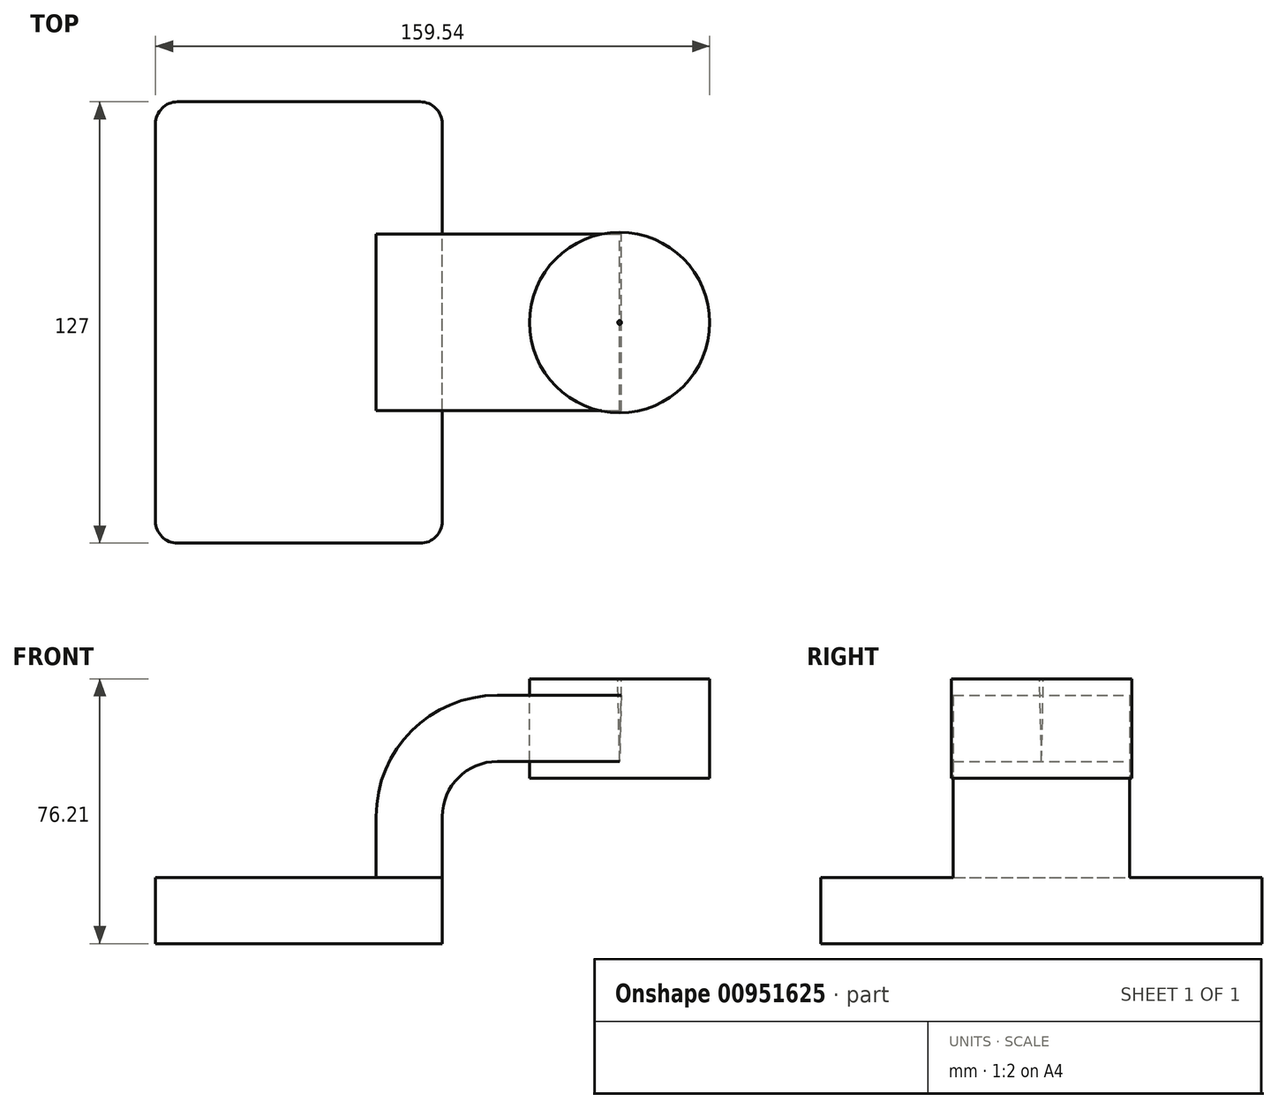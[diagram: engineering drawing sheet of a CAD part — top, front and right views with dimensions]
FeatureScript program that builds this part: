
annotation { "Feature Type Name" : "Feature", "Feature Type Description" : "" }
export const myFeature = defineFeature(function(context is Context, id is Id, definition is map)
    precondition{}
    {
        {
            var Q0;
            Q0=qCreatedBy(makeId("Front.planeOp"),FACE);
            var sketch = newSketch(context, id + "F0", { "sketchPlane" : qUnion([Q0])});
            skLineSegment(sketch, "E0.bottom", {"start": v(41.27, 9.53) * mm, "end": v(-41.28, 9.53) * mm});
            skLineSegment(sketch, "E0.top", {"start": v(41.28, -9.52) * mm, "end": v(-41.27, -9.52) * mm});
            skLineSegment(sketch, "E0.left", {"start": v(41.28, 9.53) * mm, "end": v(41.28, -9.52) * mm});
            skLineSegment(sketch, "E0.right", {"start": v(-41.28, 9.53) * mm, "end": v(-41.27, -9.52) * mm});
            skPoint(sketch, "E0.middle", {"position": v(0, 0) * mm});
            skLineSegment(sketch, "E1.bottom", {"start": v(118.27, 66.68) * mm, "end": v(67.47, 66.68) * mm});
            skLineSegment(sketch, "E1.top", {"start": v(118.27, 38.1) * mm, "end": v(67.47, 38.1) * mm});
            skLineSegment(sketch, "E1.left", {"start": v(118.27, 66.68) * mm, "end": v(118.27, 38.1) * mm});
            skLineSegment(sketch, "E1.right", {"start": v(67.47, 66.68) * mm, "end": v(67.47, 38.1) * mm});
            skPoint(sketch, "E1.middle", {"position": v(92.87, 52.39) * mm});
            skLineSegment(sketch, "E2", {"start": v(41.27, 9.53) * mm, "end": v(41.27, 27) * mm});
            skArc(sketch, "E3", {"start": v(41.27, 27) * mm, "mid": v(45.92, 38.23) * mm, "end": v(57.15, 42.88) * mm});
            skLineSegment(sketch, "E4", {"start": v(57.15, 42.88) * mm, "end": v(92.33, 42.88) * mm});
            skLineSegment(sketch, "E5.0", {"start": v(57.15, 61.93) * mm, "end": v(92.87, 61.93) * mm});
            skArc(sketch, "E5.1", {"start": v(22.23, 27) * mm, "mid": v(32.45, 51.7) * mm, "end": v(57.15, 61.93) * mm});
            skLineSegment(sketch, "E5.2", {"start": v(22.23, 9.53) * mm, "end": v(22.23, 27) * mm});
            skPoint(sketch, "E6", {"position": v(92.87, 66.68) * mm});
            skLineSegment(sketch, "E7", {"start": v(92.87, 66.68) * mm, "end": v(92.33, 42.88) * mm});
            skFitSpline(sketch, "E8", {"points": [v(57.15, 61.93) * mm, v(-41.28, 9.52) * mm], "startDerivative": vector(-71.57, 1.8) * mm, "endDerivative": vector(-45.9, -102.26) * mm});
            skLineSegment(sketch, "E9", {"start": v(92.33, 42.88) * mm, "end": v(92.33, 38.1) * mm});
            skSolve(sketch);
        }
        {
            var Q0;
            Q0=makeQuery(id+"F0.imprint","IMPRINT",FACE,{"disambiguationData":[TD([[makeQuery(id+"F0.imprint","IMPRINT",EDGE,{"derivedFrom":sQuery(id+"F0.wireOp",EDGE,"E0.top")}),-1.0]])]});
            extrude(context, id + "F1", {"entities" : qUnion([Q0]), "endBound" : BoundingType.SYMMETRIC, "depth" : 127 * mm, "offsetDistance" : 25.4 * mm});
        }
        {
            var Q0;
            {var subQ1=sQuery(id+"F0.wireOp",EDGE,"E2");Q0=makeQuery(id+"F0.imprint","IMPRINT",FACE,{"disambiguationData":[TD([[makeQuery(id+"F0.imprint","IMPRINT",EDGE,{"derivedFrom":subQ1}),1.0]])]});}
            var Q1;
            {var subQ0=sQuery(id+"F0.wireOp",EDGE,"E5.0");var subQ1=sQuery(id+"F0.wireOp",EDGE,"E1.right");var subQ2=makeQuery(id+"F0.imprint","INTERSECT",VERTEX,{"derivedFrom":[subQ1,subQ0]});Q1=makeQuery(id+"F0.imprint","IMPRINT",FACE,{"disambiguationData":[TD([[makeQuery(id+"F0.imprint","IMPRINT",EDGE,{"disambiguationData":[TD([[subQ2,-1.0]])],"derivedFrom":subQ1}),1.0]])]});}
            extrude(context, id + "F2", {"entities" : qUnion([Q0, Q1]), "operationType" : NewBodyOperationType.ADD, "endBound" : BoundingType.SYMMETRIC, "depth" : 50.8 * mm, "offsetDistance" : 25.4 * mm});
        }
        {
            var Q0;
            Q0=makeQuery(id+"F0.imprint","IMPRINT",FACE,{"disambiguationData":[TD([[makeQuery(id+"F0.imprint","IMPRINT",EDGE,{"derivedFrom":sQuery(id+"F0.wireOp",EDGE,"E5.1")}),1.0]])]});
            extrude(context, id + "F3", {"entities" : qUnion([Q0]), "operationType" : NewBodyOperationType.ADD, "endBound" : BoundingType.SYMMETRIC, "depth" : 15.88 * mm, "offsetDistance" : 25.4 * mm});
        }
        {
            var Q0;
            {var subQ4=sQuery(id+"F0.wireOp",EDGE,"E1.left");Q0=makeQuery(id+"F0.imprint","IMPRINT",FACE,{"disambiguationData":[TD([[makeQuery(id+"F0.imprint","IMPRINT",EDGE,{"derivedFrom":subQ4}),-1.0]])]});}
            var Q1;
            Q1=sQuery(id+"F0.wireOp",EDGE,"E9");
            revolve(context, id + "F4", {"surfaceOperationType" : NewSurfaceOperationType.NEW, "entities" : qUnion([Q0]), "axis" : qUnion([Q1]), "revolveType" : RevolveType.FULL});
        }
        {
            var Q0;
            Q0=makeQuery(id+"F1.opExtrude","CAP_EDGE",EDGE,{"disambiguationData":[OSD([sQuery(id+"F0.wireOp",EDGE,"E0.left")])],"isStart":false});
            var Q1;
            Q1=makeQuery(id+"F1.opExtrude","CAP_EDGE",EDGE,{"disambiguationData":[OSD([sQuery(id+"F0.wireOp",EDGE,"E0.right")])],"isStart":false});
            var Q2;
            Q2=makeQuery(id+"F1.opExtrude","CAP_EDGE",EDGE,{"disambiguationData":[OSD([sQuery(id+"F0.wireOp",EDGE,"E0.right")])],"isStart":true});
            var Q3;
            Q3=makeQuery(id+"F1.opExtrude","CAP_EDGE",EDGE,{"disambiguationData":[OSD([sQuery(id+"F0.wireOp",EDGE,"E0.left")])],"isStart":true});
            fillet(context, id + "F5", {"entities" : qUnion([Q0, Q1, Q2, Q3]), "radius" : 6.35 * mm, "tangentPropagation" : true, "allowEdgeOverflow" : false});
        }
    });
